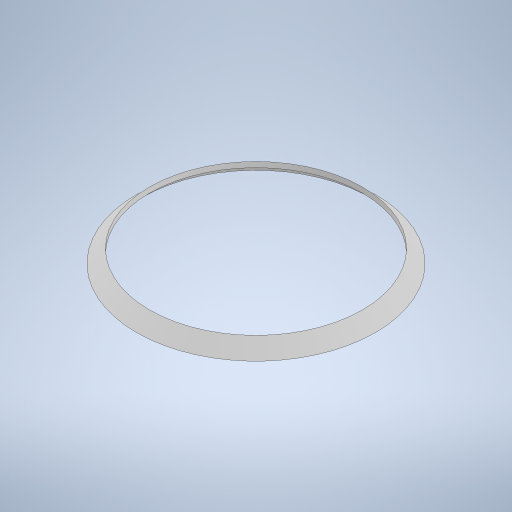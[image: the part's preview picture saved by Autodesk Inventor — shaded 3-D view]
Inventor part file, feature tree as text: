
AUTODESK INVENTOR PART (.ipt)
format: ipt  version: 2024.3 (Build 283343000, 343)  size: 247,296 bytes
history: native  units: mm
features: revolve x1, sketch x1
ambient origin geometry x8: Origin, YZ Plane, XZ Plane, XY Plane, X Axis, Y Axis, Z Axis, Center Point
bodies: Solid1 (feature_tree)
feature tree (2):
  revolve  "Revolution1"  [1 undecoded]
  sketch  "Sketch1"  dims[d0=57.0mm d1=7.0mm d2=2.0mm d3=7.0mm d4=135.0deg d5=90.0deg]
note: 1 required parameter value undecoded (feature->parameter linkage not recoverable at this tier; creation-order binding heuristic only, values carry confidence <= 0.55)
